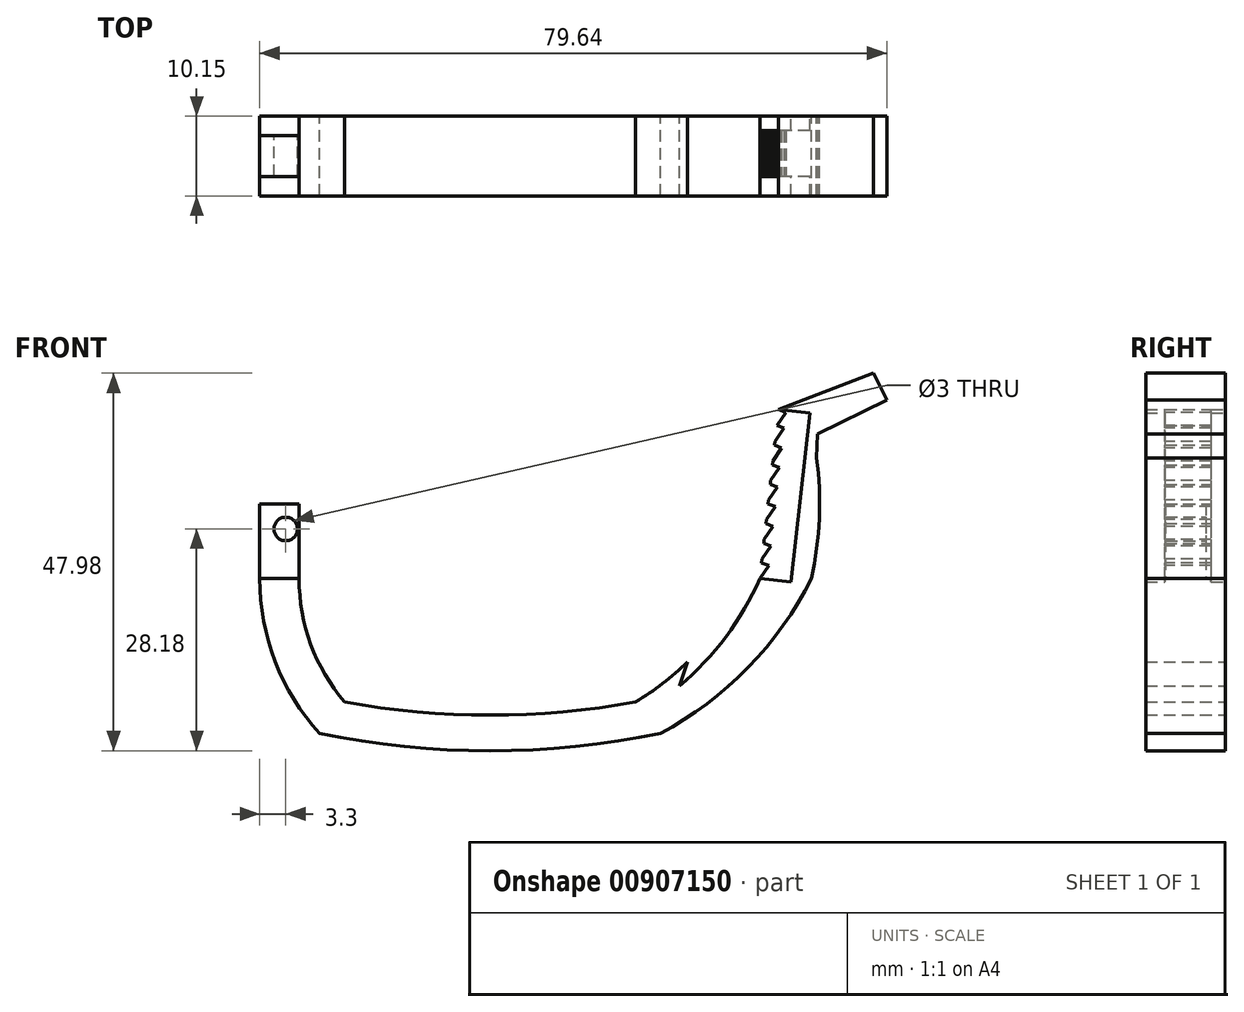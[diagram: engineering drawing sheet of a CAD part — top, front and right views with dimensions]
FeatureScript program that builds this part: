
annotation { "Feature Type Name" : "Feature", "Feature Type Description" : "" }
export const myFeature = defineFeature(function(context is Context, id is Id, definition is map)
    precondition{}
    {
        {
            var Q0;
            Q0=qCreatedBy(makeId("Front.planeOp"),FACE);
            var sketch = newSketch(context, id + "F0", { "sketchPlane" : qUnion([Q0])});
            skArc(sketch, "E0", {"start": v(-24.25, 0) * mm, "mid": v(-22.77, -8.35) * mm, "end": v(-18.5, -15.68) * mm});
            skArc(sketch, "E1", {"start": v(-18.5, -15.68) * mm, "mid": v(0, -17.35) * mm, "end": v(18.5, -15.68) * mm});
            skArc(sketch, "E2", {"start": v(18.5, -15.68) * mm, "mid": v(21.93, -13.33) * mm, "end": v(25.06, -10.6) * mm});
            skLineSegment(sketch, "E3", {"start": v(-24.25, 0) * mm, "end": v(-29.25, 0) * mm});
            skArc(sketch, "E4", {"start": v(-29.25, 0) * mm, "mid": v(-27.28, -10.55) * mm, "end": v(-21.64, -19.68) * mm});
            skArc(sketch, "E5", {"start": v(-21.64, -19.68) * mm, "mid": v(0, -21.88) * mm, "end": v(21.64, -19.68) * mm});
            skArc(sketch, "E6", {"start": v(21.64, -19.68) * mm, "mid": v(32.76, -11.32) * mm, "end": v(40.85, 0) * mm});
            skArc(sketch, "E7", {"start": v(34.28, 0) * mm, "mid": v(29.97, -7.4) * mm, "end": v(24.1, -13.62) * mm});
            skLineSegment(sketch, "E8", {"start": v(25.06, -10.6) * mm, "end": v(24.1, -13.62) * mm});
            skArc(sketch, "E9", {"start": v(40.85, 0) * mm, "mid": v(41.82, 7.63) * mm, "end": v(41.5, 15.32) * mm});
            skLineSegment(sketch, "E10", {"start": v(50.39, 22.7) * mm, "end": v(48.72, 26.1) * mm});
            skLineSegment(sketch, "E11", {"start": v(50.39, 22.7) * mm, "end": v(41.58, 18.38) * mm});
            skLineSegment(sketch, "E12", {"start": v(41.58, 18.38) * mm, "end": v(41.5, 15.32) * mm});
            skLineSegment(sketch, "E13", {"start": v(34.28, 0) * mm, "end": v(36.65, 21.46) * mm});
            skLineSegment(sketch, "E14", {"start": v(48.72, 26.1) * mm, "end": v(36.65, 21.46) * mm});
            skSolve(sketch);
        }
        {
            var Q0;
            Q0 = qSketchRegion(id + "F0", true);
            extrude(context, id + "F1", {"entities" : qUnion([Q0]), "depth" : 10.15 * mm, "offsetDistance" : 25 * mm});
        }
        {
            var Q0;
            Q0=makeQuery(id+"F1.opExtrude","SWEPT_FACE",FACE,{"disambiguationData":[OSD([sQuery(id+"F0.wireOp",EDGE,"E13")])]});
            var sketch = newSketch(context, id + "F2", { "sketchPlane" : qUnion([Q0])});
            skLineSegment(sketch, "E15.bottom", {"start": v(0, 25.36) * mm, "end": v(1.85, 25.36) * mm});
            skLineSegment(sketch, "E15.top", {"start": v(0, 3.77) * mm, "end": v(1.85, 3.77) * mm});
            skLineSegment(sketch, "E15.left", {"start": v(0, 25.36) * mm, "end": v(0, 3.77) * mm});
            skLineSegment(sketch, "E15.right", {"start": v(1.85, 25.36) * mm, "end": v(1.85, 3.77) * mm});
            skLineSegment(sketch, "E16.bottom", {"start": v(10.15, 25.36) * mm, "end": v(7.7, 25.36) * mm});
            skLineSegment(sketch, "E16.top", {"start": v(10.15, 3.77) * mm, "end": v(7.7, 3.77) * mm});
            skLineSegment(sketch, "E16.left", {"start": v(10.15, 25.36) * mm, "end": v(10.15, 3.77) * mm});
            skLineSegment(sketch, "E16.right", {"start": v(7.7, 25.36) * mm, "end": v(7.7, 3.77) * mm});
            skSolve(sketch);
        }
        {
            var Q0;
            Q0 = qSketchRegion(id + "F2", true);
            extrude(context, id + "F3", {"entities" : qUnion([Q0]), "operationType" : NewBodyOperationType.REMOVE, "oppositeDirection" : true, "depth" : 4 * mm, "offsetDistance" : 25 * mm});
        }
        {
            var Q0;
            Q0=makeQuery(id+"F3.boolean.opBoolean","COPY",FACE,{"derivedFrom":makeQuery(id+"F3.opExtrude","SWEPT_FACE",FACE,{"disambiguationData":[OSD([sQuery(id+"F2.wireOp",EDGE,"E16.right")])]})});
            var sketch = newSketch(context, id + "F4", { "sketchPlane" : qUnion([Q0])});
            skLineSegment(sketch, "E17", {"start": v(36.65, 21.46) * mm, "end": v(36.43, 19.46) * mm});
            skLineSegment(sketch, "E18", {"start": v(36.43, 19.46) * mm, "end": v(37.58, 21.1) * mm});
            skLineSegment(sketch, "E19", {"start": v(37.58, 21.1) * mm, "end": v(36.65, 21.46) * mm});
            skPoint(sketch, "E20", {"position": v(36.38, 18.96) * mm});
            skLineSegment(sketch, "E21", {"start": v(36.38, 19.44) * mm, "end": v(36.2, 17.44) * mm});
            skLineSegment(sketch, "E22", {"start": v(36.2, 17.44) * mm, "end": v(37.32, 19.1) * mm});
            skLineSegment(sketch, "E23", {"start": v(37.32, 19.1) * mm, "end": v(36.38, 19.44) * mm});
            skPoint(sketch, "E24", {"position": v(36.1, 16.44) * mm});
            skLineSegment(sketch, "E25", {"start": v(36.11, 16.95) * mm, "end": v(35.93, 14.95) * mm});
            skLineSegment(sketch, "E26", {"start": v(35.93, 14.95) * mm, "end": v(37.05, 16.6) * mm});
            skLineSegment(sketch, "E27", {"start": v(37.05, 16.6) * mm, "end": v(36.11, 16.95) * mm});
            skLineSegment(sketch, "E28", {"start": v(35.84, 14.46) * mm, "end": v(35.66, 12.46) * mm});
            skLineSegment(sketch, "E29", {"start": v(35.66, 12.46) * mm, "end": v(36.78, 14.12) * mm});
            skLineSegment(sketch, "E30", {"start": v(36.78, 14.12) * mm, "end": v(35.84, 14.46) * mm});
            skLineSegment(sketch, "E31", {"start": v(35.56, 11.97) * mm, "end": v(35.38, 9.97) * mm});
            skLineSegment(sketch, "E32", {"start": v(35.38, 9.97) * mm, "end": v(36.5, 11.63) * mm});
            skLineSegment(sketch, "E33", {"start": v(36.5, 11.63) * mm, "end": v(35.56, 11.97) * mm});
            skLineSegment(sketch, "E34", {"start": v(35.3, 9.48) * mm, "end": v(35.1, 7.48) * mm});
            skLineSegment(sketch, "E35", {"start": v(35.1, 7.48) * mm, "end": v(36.23, 9.13) * mm});
            skLineSegment(sketch, "E36", {"start": v(36.23, 9.13) * mm, "end": v(35.3, 9.48) * mm});
            skLineSegment(sketch, "E37", {"start": v(35, 6.99) * mm, "end": v(34.83, 4.99) * mm});
            skLineSegment(sketch, "E38", {"start": v(34.83, 4.99) * mm, "end": v(35.95, 6.65) * mm});
            skLineSegment(sketch, "E39", {"start": v(35.95, 6.65) * mm, "end": v(35, 6.99) * mm});
            skLineSegment(sketch, "E40", {"start": v(34.73, 4.5) * mm, "end": v(34.55, 2.5) * mm});
            skLineSegment(sketch, "E41", {"start": v(34.55, 2.5) * mm, "end": v(35.67, 4.16) * mm});
            skLineSegment(sketch, "E42", {"start": v(35.67, 4.16) * mm, "end": v(34.73, 4.5) * mm});
            skLineSegment(sketch, "E43", {"start": v(34.5, 2) * mm, "end": v(34.28, 0) * mm});
            skLineSegment(sketch, "E44", {"start": v(34.28, 0) * mm, "end": v(35.43, 1.63) * mm});
            skLineSegment(sketch, "E45", {"start": v(35.43, 1.63) * mm, "end": v(34.5, 2) * mm});
            skSolve(sketch);
        }
        {
            var Q0;
            Q0=makeQuery(id+"F4.imprint","IMPRINT",FACE,{"disambiguationData":[TD([[makeQuery(id+"F4.imprint","IMPRINT",EDGE,{"derivedFrom":sQuery(id+"F4.wireOp",EDGE,"E43")}),1.0]])]});
            var Q1;
            {var subQ0=sQuery(id+"F4.wireOp",EDGE,"E21");Q1=makeQuery(id+"F4.imprint","IMPRINT",FACE,{"disambiguationData":[TD([[makeQuery(id+"F4.imprint","IMPRINT",EDGE,{"derivedFrom":subQ0}),1.0]])]});}
            var Q2;
            {var subQ0=sQuery(id+"F4.wireOp",EDGE,"E25");Q2=makeQuery(id+"F4.imprint","IMPRINT",FACE,{"disambiguationData":[TD([[makeQuery(id+"F4.imprint","IMPRINT",EDGE,{"derivedFrom":subQ0}),1.0]])]});}
            var Q3;
            {var subQ0=sQuery(id+"F4.wireOp",EDGE,"E28");Q3=makeQuery(id+"F4.imprint","IMPRINT",FACE,{"disambiguationData":[TD([[makeQuery(id+"F4.imprint","IMPRINT",EDGE,{"derivedFrom":subQ0}),1.0]])]});}
            var Q4;
            {var subQ0=sQuery(id+"F4.wireOp",EDGE,"E31");Q4=makeQuery(id+"F4.imprint","IMPRINT",FACE,{"disambiguationData":[TD([[makeQuery(id+"F4.imprint","IMPRINT",EDGE,{"derivedFrom":subQ0}),1.0]])]});}
            var Q5;
            {var subQ0=sQuery(id+"F4.wireOp",EDGE,"E34");Q5=makeQuery(id+"F4.imprint","IMPRINT",FACE,{"disambiguationData":[TD([[makeQuery(id+"F4.imprint","IMPRINT",EDGE,{"derivedFrom":subQ0}),1.0]])]});}
            var Q6;
            {var subQ0=sQuery(id+"F4.wireOp",EDGE,"E37");Q6=makeQuery(id+"F4.imprint","IMPRINT",FACE,{"disambiguationData":[TD([[makeQuery(id+"F4.imprint","IMPRINT",EDGE,{"derivedFrom":subQ0}),1.0]])]});}
            var Q7;
            {var subQ0=sQuery(id+"F4.wireOp",EDGE,"E40");Q7=makeQuery(id+"F4.imprint","IMPRINT",FACE,{"disambiguationData":[TD([[makeQuery(id+"F4.imprint","IMPRINT",EDGE,{"derivedFrom":subQ0}),1.0]])]});}
            var Q8;
            {var subQ0=sQuery(id+"F4.wireOp",EDGE,"E26");Q8=makeQuery(id+"F4.imprint","IMPRINT",FACE,{"disambiguationData":[TD([[makeQuery(id+"F4.imprint","IMPRINT",EDGE,{"derivedFrom":subQ0}),1.0]])]});}
            var Q9;
            {var subQ0=sQuery(id+"F4.wireOp",EDGE,"E29");Q9=makeQuery(id+"F4.imprint","IMPRINT",FACE,{"disambiguationData":[TD([[makeQuery(id+"F4.imprint","IMPRINT",EDGE,{"derivedFrom":subQ0}),1.0]])]});}
            var Q10;
            {var subQ0=sQuery(id+"F4.wireOp",EDGE,"E32");Q10=makeQuery(id+"F4.imprint","IMPRINT",FACE,{"disambiguationData":[TD([[makeQuery(id+"F4.imprint","IMPRINT",EDGE,{"derivedFrom":subQ0}),1.0]])]});}
            var Q11;
            {var subQ0=sQuery(id+"F4.wireOp",EDGE,"E35");Q11=makeQuery(id+"F4.imprint","IMPRINT",FACE,{"disambiguationData":[TD([[makeQuery(id+"F4.imprint","IMPRINT",EDGE,{"derivedFrom":subQ0}),1.0]])]});}
            var Q12;
            {var subQ0=sQuery(id+"F4.wireOp",EDGE,"E38");Q12=makeQuery(id+"F4.imprint","IMPRINT",FACE,{"disambiguationData":[TD([[makeQuery(id+"F4.imprint","IMPRINT",EDGE,{"derivedFrom":subQ0}),1.0]])]});}
            var Q13;
            {var subQ0=sQuery(id+"F4.wireOp",EDGE,"E41");Q13=makeQuery(id+"F4.imprint","IMPRINT",FACE,{"disambiguationData":[TD([[makeQuery(id+"F4.imprint","IMPRINT",EDGE,{"derivedFrom":subQ0}),1.0]])]});}
            var Q14;
            Q14=makeQuery(id+"F4.imprint","IMPRINT",FACE,{"disambiguationData":[TD([[makeQuery(id+"F4.imprint","IMPRINT",EDGE,{"derivedFrom":sQuery(id+"F4.wireOp",EDGE,"E17")}),1.0]])]});
            var Q15;
            {var subQ0=sQuery(id+"F4.wireOp",EDGE,"E22");Q15=makeQuery(id+"F4.imprint","IMPRINT",FACE,{"disambiguationData":[TD([[makeQuery(id+"F4.imprint","IMPRINT",EDGE,{"derivedFrom":subQ0}),1.0]])]});}
            extrude(context, id + "F5", {"entities" : qUnion([Q0, Q1, Q2, Q3, Q4, Q5, Q6, Q7, Q8, Q9, Q10, Q11, Q12, Q13, Q14, Q15]), "operationType" : NewBodyOperationType.REMOVE, "endBound" : BoundingType.THROUGH_ALL, "oppositeDirection" : true, "depth" : 25 * mm, "offsetDistance" : 25 * mm});
        }
        {
            var Q0;
            Q0=makeQuery(id+"F1.opExtrude","SWEPT_FACE",FACE,{"disambiguationData":[OSD([sQuery(id+"F0.wireOp",EDGE,"E3")])]});
            var sketch = newSketch(context, id + "F6", { "sketchPlane" : qUnion([Q0])});
            skLineSegment(sketch, "E46.bottom", {"start": v(-24.25, -7.65) * mm, "end": v(-29.25, -7.65) * mm});
            skLineSegment(sketch, "E46.top", {"start": v(-24.25, -2.5) * mm, "end": v(-29.25, -2.5) * mm});
            skLineSegment(sketch, "E46.left", {"start": v(-24.25, -7.65) * mm, "end": v(-24.25, -2.5) * mm});
            skLineSegment(sketch, "E46.right", {"start": v(-29.25, -7.65) * mm, "end": v(-29.25, -2.5) * mm});
            skSolve(sketch);
        }
        {
            var Q0;
            Q0=makeQuery(id+"F6.imprint","IMPRINT",FACE,{"disambiguationData":[TD([[makeQuery(id+"F6.imprint","IMPRINT",EDGE,{"derivedFrom":sQuery(id+"F6.wireOp",EDGE,"E46.bottom")}),-1.0]])]});
            extrude(context, id + "F7", {"entities" : qUnion([Q0]), "operationType" : NewBodyOperationType.ADD, "depth" : 9.5 * mm, "offsetDistance" : 25 * mm});
        }
        {
            var Q0;
            Q0=makeQuery(id+"F7.opExtrude","SWEPT_FACE",FACE,{"disambiguationData":[OSD([sQuery(id+"F6.wireOp",EDGE,"E46.top")])]});
            var sketch = newSketch(context, id + "F8", { "sketchPlane" : qUnion([Q0])});
            skCircle(sketch, "E47", {"center": v(25.95, 6.3) * mm, "radius": 1.5 * mm});
            skSolve(sketch);
        }
        {
            var Q0;
            Q0 = qSketchRegion(id + "F8", true);
            extrude(context, id + "F9", {"entities" : qUnion([Q0]), "operationType" : NewBodyOperationType.REMOVE, "endBound" : BoundingType.THROUGH_ALL, "oppositeDirection" : true, "depth" : 25 * mm, "offsetDistance" : 25 * mm});
        }
    });
